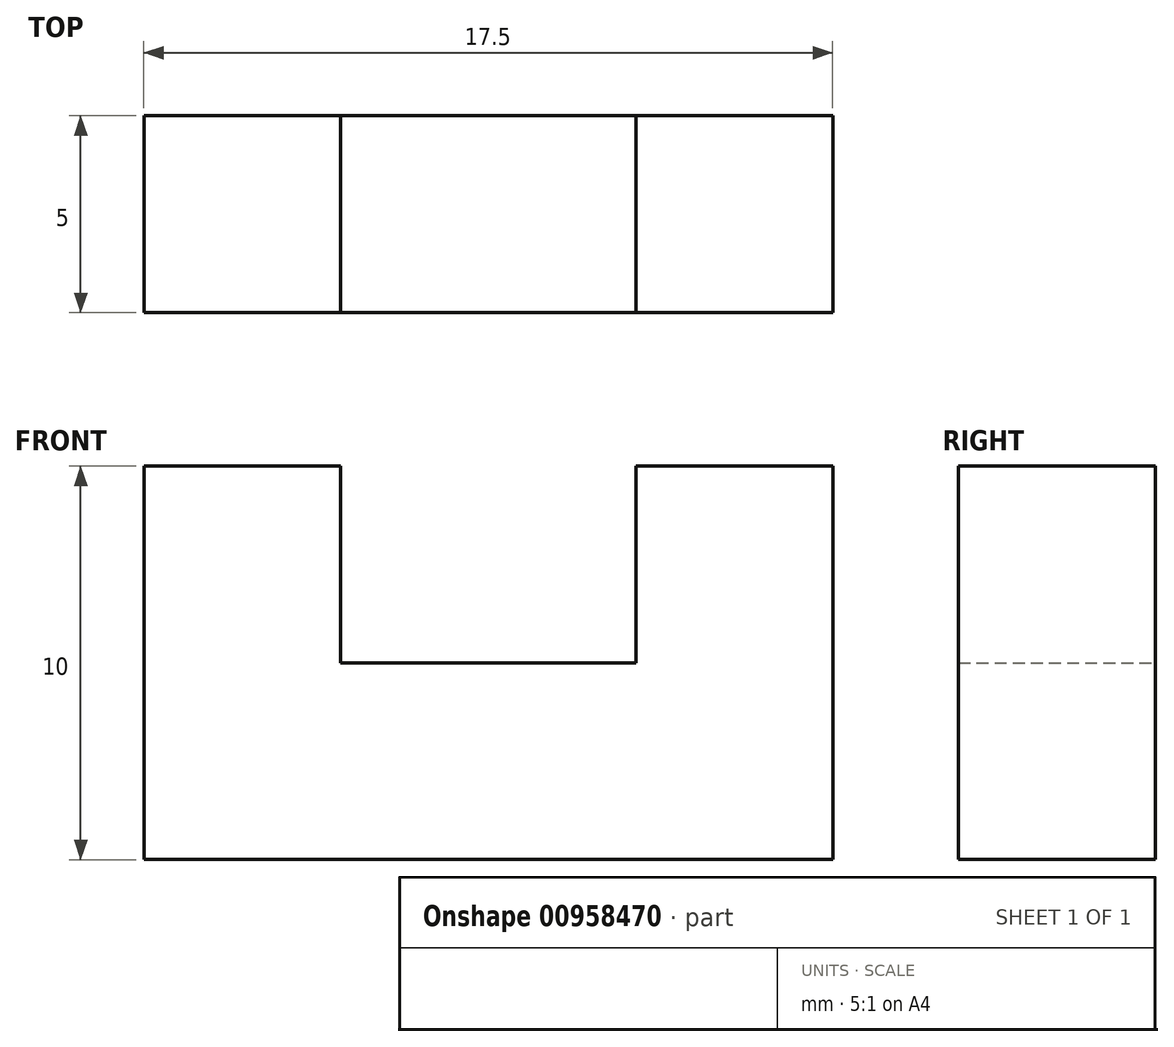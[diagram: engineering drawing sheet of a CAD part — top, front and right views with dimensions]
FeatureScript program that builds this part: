
annotation { "Feature Type Name" : "Feature", "Feature Type Description" : "" }
export const myFeature = defineFeature(function(context is Context, id is Id, definition is map)
    precondition{}
    {
        {
            var Q0;
            Q0=qCreatedBy(makeId("Front.planeOp"),FACE);
            var sketch = newSketch(context, id + "F0", { "sketchPlane" : qUnion([Q0])});
            skLineSegment(sketch, "E0", {"start": v(-38.97, 18.34) * mm, "end": v(-33.97, 18.34) * mm});
            skLineSegment(sketch, "E1", {"start": v(-33.97, 18.34) * mm, "end": v(-33.97, 13.34) * mm});
            skLineSegment(sketch, "E2", {"start": v(-33.97, 13.34) * mm, "end": v(-26.47, 13.34) * mm});
            skLineSegment(sketch, "E3", {"start": v(-26.47, 13.34) * mm, "end": v(-26.47, 18.34) * mm});
            skLineSegment(sketch, "E4", {"start": v(-26.47, 18.34) * mm, "end": v(-21.47, 18.34) * mm});
            skLineSegment(sketch, "E5", {"start": v(-21.47, 18.34) * mm, "end": v(-21.47, 8.34) * mm});
            skLineSegment(sketch, "E6", {"start": v(-21.47, 8.34) * mm, "end": v(-38.97, 8.34) * mm});
            skLineSegment(sketch, "E7", {"start": v(-38.97, 8.34) * mm, "end": v(-38.97, 18.34) * mm});
            skSolve(sketch);
        }
        {
            var Q0;
            Q0 = qSketchRegion(id + "F0", true);
            extrude(context, id + "F1", {"entities" : qUnion([Q0]), "depth" : 5 * mm, "offsetDistance" : 25 * mm});
        }
    });
